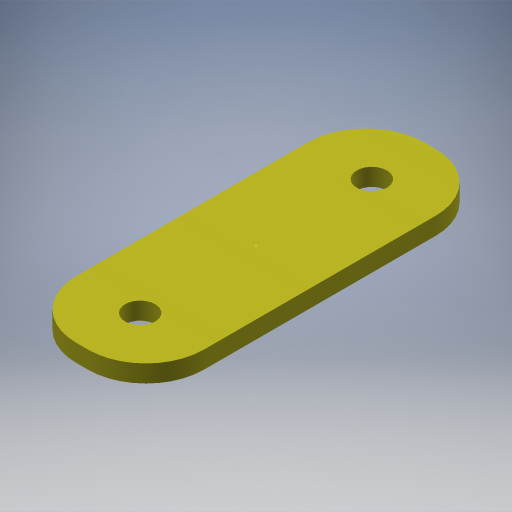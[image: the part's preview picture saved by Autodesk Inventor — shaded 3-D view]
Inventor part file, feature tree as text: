
AUTODESK INVENTOR PART (.ipt)
format: ipt  version: 2024.3 (Build 283343000, 343)  size: 254,464 bytes
history: native  units: mm
features: sketch x2, extrude x1, hole x1, fillet x1, projected_geometry x1
ambient origin geometry x8: Origin, YZ Plane, XZ Plane, XY Plane, X Axis, Y Axis, Z Axis, Center Point
bodies: Volumenkörper1 (feature_tree)
feature tree (6):
  extrude  "Extrusion1"  Depth=22.0mm
  hole  "Bohrung1"  [1 undecoded]
  fillet  "Rundung1"  Radius=10.0mm
  sketch  "Skizze3"  dims[d2=3.0mm d3=0.0mm d4=40.0mm d5=5.2mm d6=6.0mm d7=4.0mm d8=2.0mm d9=90.0deg d10=8.8mm d11=20.594885mm d12=10.0mm]
  sketch  "Skizze2"  dims[d0=60.0mm d1=22.0mm]
  projected_geometry  "Projizierte Kontur1"
note: 1 required parameter value undecoded (feature->parameter linkage not recoverable at this tier; creation-order binding heuristic only, values carry confidence <= 0.55)
